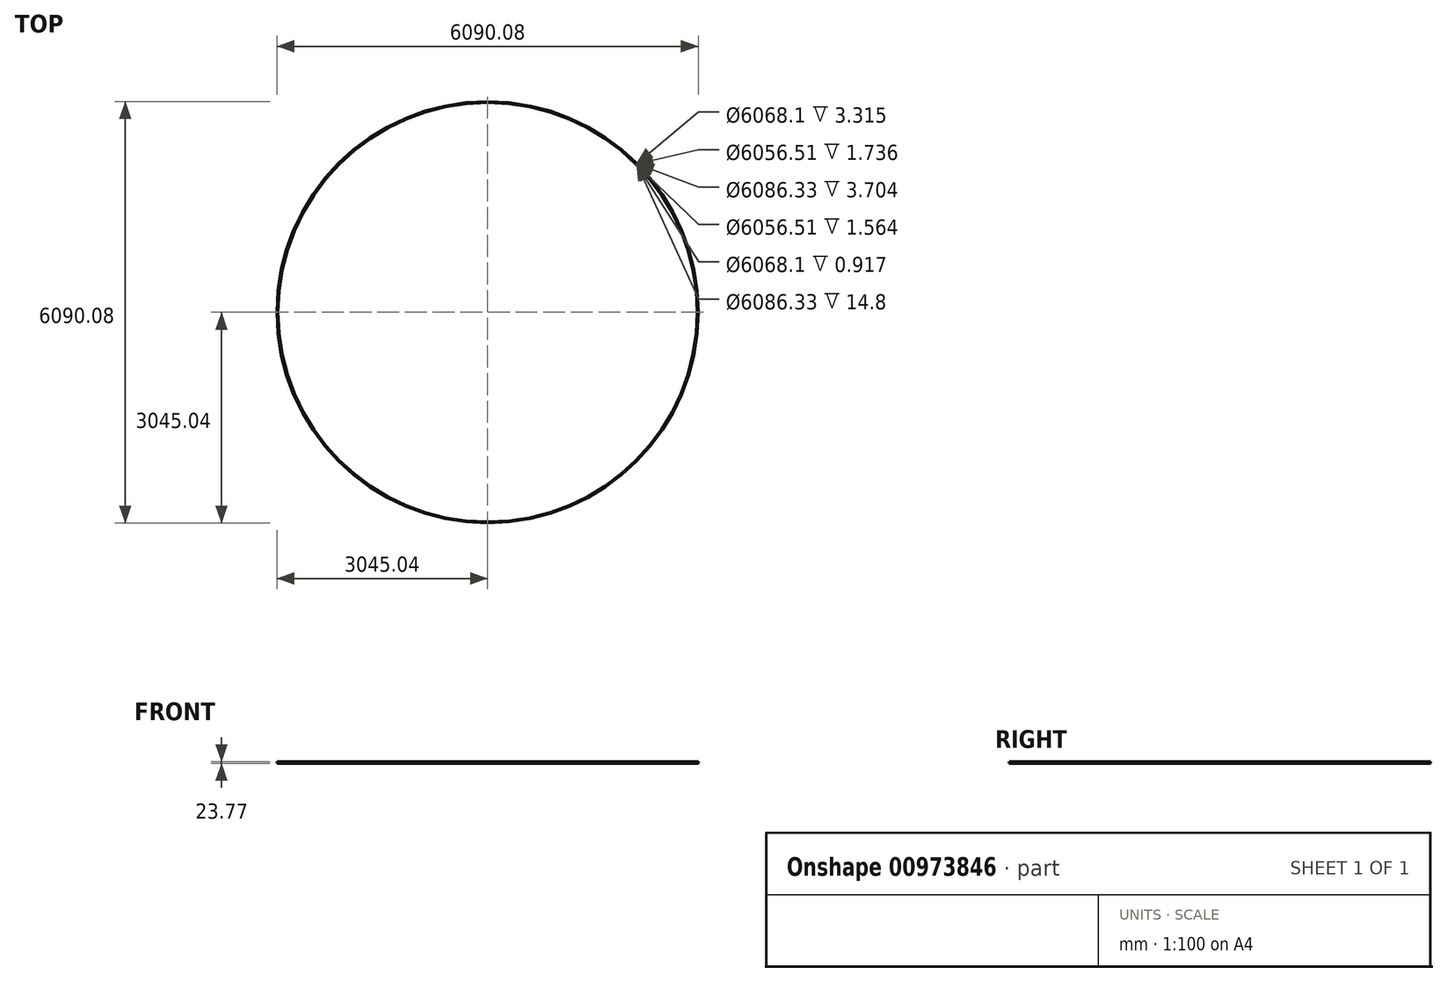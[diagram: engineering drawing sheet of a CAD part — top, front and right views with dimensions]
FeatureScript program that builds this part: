
annotation { "Feature Type Name" : "Feature", "Feature Type Description" : "" }
export const myFeature = defineFeature(function(context is Context, id is Id, definition is map)
    precondition{}
    {
        {
            var Q0;
            Q0=qCreatedBy(makeId("Front.planeOp"),FACE);
            var sketch = newSketch(context, id + "F0", { "sketchPlane" : qUnion([Q0])});
            skLineSegment(sketch, "E0", {"start": v(0, 11.38) * mm, "end": v(0, -12.39) * mm});
            skLineSegment(sketch, "E1.MirrorCS", {"start": v(11, -10.42) * mm, "end": v(11, -12.39) * mm});
            skLineSegment(sketch, "E2.MirrorCS", {"start": v(9.34, 3.46) * mm, "end": v(9.34, 4.38) * mm});
            skLineSegment(sketch, "E3.MirrorCS", {"start": v(11, 4.38) * mm, "end": v(11, 3.46) * mm});
            skLineSegment(sketch, "E4.MirrorCS", {"start": v(1.88, -10.42) * mm, "end": v(9.34, -10.42) * mm});
            skLineSegment(sketch, "E5.MirrorCS", {"start": v(9.34, 4.38) * mm, "end": v(1.88, 4.38) * mm});
            skLineSegment(sketch, "E6.MirrorCS", {"start": v(9.34, -9.07) * mm, "end": v(11, -9.07) * mm});
            skLineSegment(sketch, "E7.MirrorCS", {"start": v(9.34, -10.42) * mm, "end": v(9.34, -9.07) * mm});
            skLineSegment(sketch, "E8.MirrorCS", {"start": v(11, -12.39) * mm, "end": v(0, -12.39) * mm});
            skLineSegment(sketch, "E9.MirrorCS", {"start": v(11, 3.46) * mm, "end": v(9.34, 3.46) * mm});
            skLineSegment(sketch, "E10.MirrorCS", {"start": v(11, -9.07) * mm, "end": v(11, -10.42) * mm});
            skLineSegment(sketch, "E11.MirrorCS", {"start": v(1.88, 7.54) * mm, "end": v(1.88, 5.94) * mm});
            skLineSegment(sketch, "E12.MirrorCS", {"start": v(16.8, 4.38) * mm, "end": v(11, 4.38) * mm});
            skPoint(sketch, "E13.MirrorP", {"position": v(9.34, 7.54) * mm});
            skLineSegment(sketch, "E14.MirrorCS", {"start": v(16.8, 5.94) * mm, "end": v(16.8, 4.38) * mm});
            skLineSegment(sketch, "E15.MirrorCS", {"start": v(1.88, 5.94) * mm, "end": v(16.8, 5.94) * mm});
            skLineSegment(sketch, "E16.MirrorCS", {"start": v(1.88, 9.65) * mm, "end": v(1.88, 7.54) * mm});
            skLineSegment(sketch, "E17.MirrorCS", {"start": v(16.8, 11.38) * mm, "end": v(16.8, 9.65) * mm});
            skLineSegment(sketch, "E18.MirrorCS", {"start": v(1.88, 4.38) * mm, "end": v(1.88, -10.42) * mm});
            skLineSegment(sketch, "E19.MirrorCS", {"start": v(0, 11.38) * mm, "end": v(16.8, 11.38) * mm});
            skLineSegment(sketch, "E20.MirrorCS", {"start": v(16.8, 9.65) * mm, "end": v(1.88, 9.65) * mm});
            skSolve(sketch);
        }
        {
            var Q0;
            Q0=qCreatedBy(makeId("Top.planeOp"),FACE);
            var sketch = newSketch(context, id + "F1", { "sketchPlane" : qUnion([Q0])});
            skCircle(sketch, "E21", {"center": v(3045.05, 0) * mm, "radius": 3045 * mm});
            skSolve(sketch);
        }
        {
            var Q0;
            Q0=makeQuery(id+"F0.imprint","IMPRINT",FACE,{"disambiguationData":[TD([[makeQuery(id+"F0.imprint","IMPRINT",EDGE,{"derivedFrom":sQuery(id+"F0.wireOp",EDGE,"E0")}),1.0]])]});
            var Q1;
            Q1=sQuery(id+"F1.wireOp",EDGE,"E21");
            sweep(context, id + "F2", {"profiles" : qUnion([Q0]), "path" : qUnion([Q1])});
        }
        {
            var Q0;
            Q0=qCreatedBy(makeId("Front.planeOp"),FACE);
            var sketch = newSketch(context, id + "F3", { "sketchPlane" : qUnion([Q0])});
            skLineSegment(sketch, "E22.bottom", {"start": v(1675.18, 38.54) * mm, "end": v(2900.18, 38.54) * mm});
            skLineSegment(sketch, "E22.top", {"start": v(1675.18, -46.92) * mm, "end": v(2900.18, -46.92) * mm});
            skLineSegment(sketch, "E22.left", {"start": v(1675.18, 38.54) * mm, "end": v(1675.18, -46.92) * mm});
            skLineSegment(sketch, "E22.right", {"start": v(2900.18, 38.54) * mm, "end": v(2900.18, -46.92) * mm});
            skSolve(sketch);
        }
        {
            var Q0;
            Q0 = qSketchRegion(id + "F3", true);
            extrude(context, id + "F4", {"entities" : qUnion([Q0]), "operationType" : NewBodyOperationType.REMOVE, "depth" : 2400 * mm, "offsetDistance" : 25 * mm});
        }
    });
